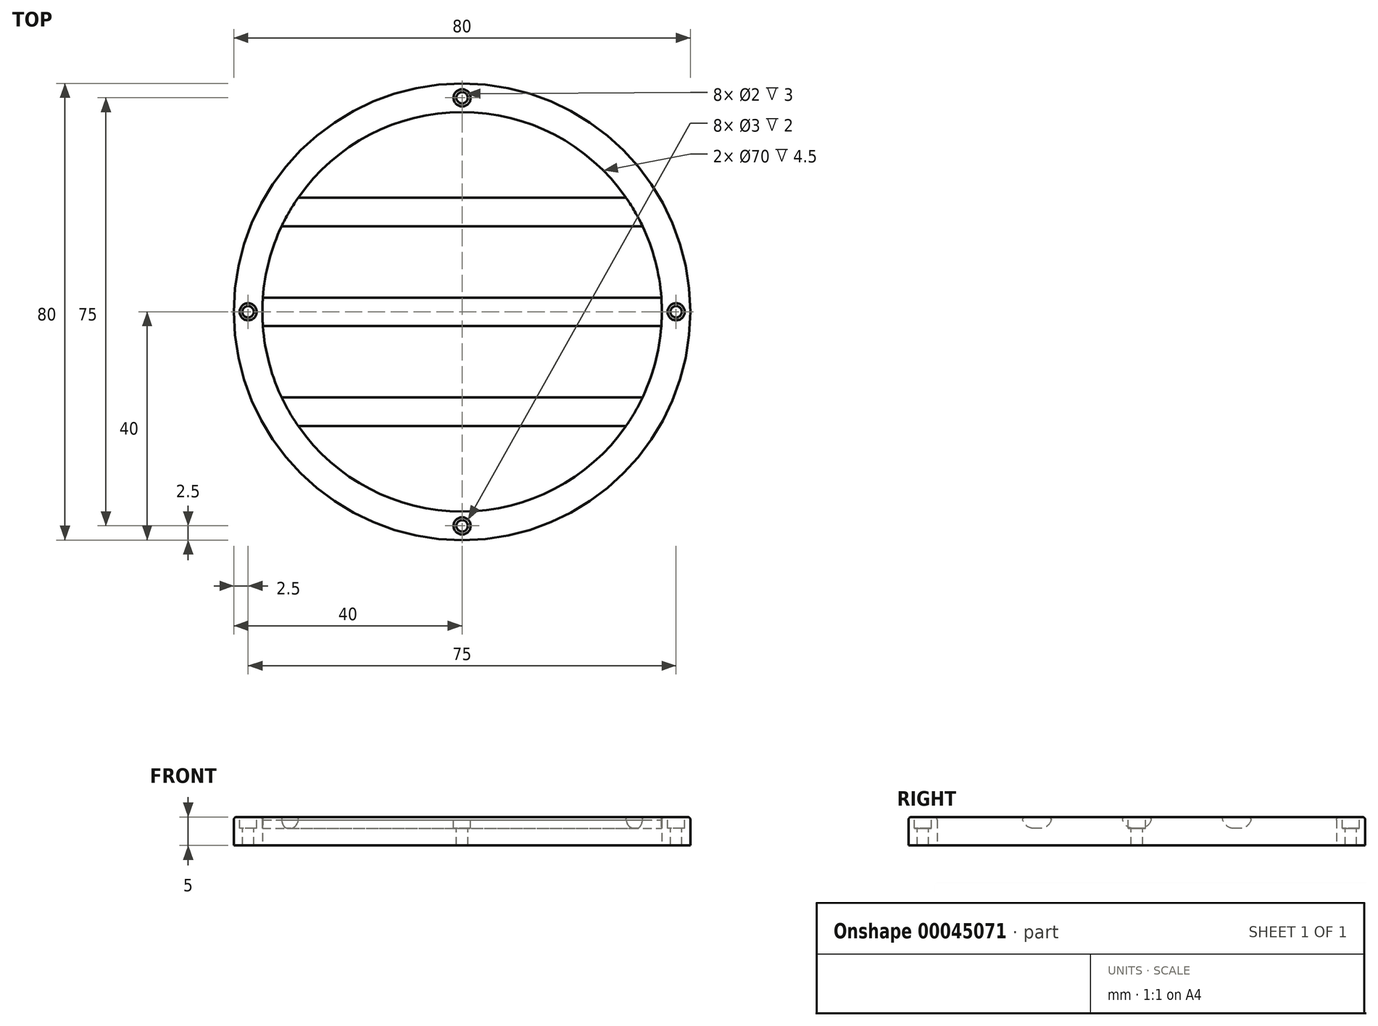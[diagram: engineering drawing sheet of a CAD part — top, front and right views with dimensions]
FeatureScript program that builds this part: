
annotation { "Feature Type Name" : "Feature", "Feature Type Description" : "" }
export const myFeature = defineFeature(function(context is Context, id is Id, definition is map)
    precondition{}
    {
        {
            var Q0;
            Q0=qCreatedBy(makeId("Top.planeOp"),FACE);
            var sketch = newSketch(context, id + "F0", { "sketchPlane" : qUnion([Q0])});
            skCircle(sketch, "E0", {"center": v(0, 0) * mm, "radius": 40 * mm});
            skCircle(sketch, "E1", {"center": v(0, 0) * mm, "radius": 35 * mm});
            skSolve(sketch);
        }
        {
            var Q0;
            Q0=makeQuery(id+"F0.imprint","IMPRINT",FACE,{"disambiguationData":[TD([[makeQuery(id+"F0.imprint","IMPRINT",EDGE,{"derivedFrom":sQuery(id+"F0.wireOp",EDGE,"E0")}),1.0]])]});
            extrude(context, id + "F1", {"entities" : qUnion([Q0]), "depth" : 5 * mm});
        }
        {
            var Q0;
            Q0=makeQuery(id+"F1.opExtrude","CAP_FACE",FACE,{"disambiguationData":[OSD([sQuery(id+"F0.wireOp",EDGE,"E0"),sQuery(id+"F0.wireOp",EDGE,"E1")])],"isStart":false});
            var sketch = newSketch(context, id + "F2", { "sketchPlane" : qUnion([Q0])});
            skLineSegment(sketch, "E2", {"start": v(-28.72, 20) * mm, "end": v(28.72, 20) * mm});
            skLineSegment(sketch, "E3", {"start": v(-31.62, 15) * mm, "end": v(31.62, 15) * mm});
            skLineSegment(sketch, "E4", {"start": v(-28.72, -20) * mm, "end": v(28.72, -20) * mm});
            skLineSegment(sketch, "E5", {"start": v(-31.62, -15) * mm, "end": v(31.62, -15) * mm});
            skLineSegment(sketch, "E6", {"start": v(-34.91, 2.5) * mm, "end": v(34.91, 2.5) * mm});
            skLineSegment(sketch, "E7", {"start": v(-34.91, -2.5) * mm, "end": v(34.91, -2.5) * mm});
            skSolve(sketch);
        }
        {
            var Q0;
            {var subQ2=sQuery(id+"F2.wireOp",EDGE,"E2");Q0=makeQuery(id+"F2.imprint","IMPRINT",FACE,{"disambiguationData":[TD([[makeQuery(id+"F2.imprint","IMPRINT",EDGE,{"derivedFrom":subQ2}),-1.0]])]});}
            var Q1;
            {var subQ2=sQuery(id+"F2.wireOp",EDGE,"E6");Q1=makeQuery(id+"F2.imprint","IMPRINT",FACE,{"disambiguationData":[TD([[makeQuery(id+"F2.imprint","IMPRINT",EDGE,{"derivedFrom":subQ2}),-1.0]])]});}
            var Q2;
            {var subQ2=sQuery(id+"F2.wireOp",EDGE,"E4");Q2=makeQuery(id+"F2.imprint","IMPRINT",FACE,{"disambiguationData":[TD([[makeQuery(id+"F2.imprint","IMPRINT",EDGE,{"derivedFrom":subQ2}),1.0]])]});}
            extrude(context, id + "F3", {"entities" : qUnion([Q0, Q1, Q2]), "oppositeDirection" : true, "depth" : 2 * mm});
        }
        {
            var Q0;
            Q0=makeQuery(id+"F1.opExtrude","CAP_FACE",FACE,{"disambiguationData":[OSD([sQuery(id+"F0.wireOp",EDGE,"E0"),sQuery(id+"F0.wireOp",EDGE,"E1")])],"isStart":false});
            var sketch = newSketch(context, id + "F4", { "sketchPlane" : qUnion([Q0])});
            skPoint(sketch, "E8", {"position": v(0, 37.5) * mm});
            skPoint(sketch, "E9", {"position": v(37.5, 0) * mm});
            skPoint(sketch, "E10", {"position": v(-37.5, 0) * mm});
            skPoint(sketch, "E11", {"position": v(0, -37.5) * mm});
            skSolve(sketch);
        }
        {
            var Q0;
            Q0=sQuery(id+"F4.wireOp",VERTEX,"E8");
            var Q1;
            Q1=sQuery(id+"F4.wireOp",VERTEX,"E9");
            var Q2;
            Q2=sQuery(id+"F4.wireOp",VERTEX,"E10");
            var Q3;
            Q3=sQuery(id+"F4.wireOp",VERTEX,"E11");
            var Q4;
            Q4=makeQuery(id+"F1.opExtrude","SWEPT_BODY",BODY,{"disambiguationData":[OSD([sQuery(id+"F0.wireOp",EDGE,"E0"),sQuery(id+"F0.wireOp",EDGE,"E1")])]});
            hole(context, id + "F5", {"style" : HoleStyle.C_BORE, "holeDiameter" : 2 * mm, "cBoreDiameter" : 3 * mm, "cBoreDepth" : 2 * mm, "endStyle" : HoleEndStyle.THROUGH, "locations" : qUnion([Q0, Q1, Q2, Q3]), "scope" : qUnion([Q4])});
        }
        {
            var Q0;
            Q0=makeQuery(id+"F1.opExtrude","CAP_EDGE",EDGE,{"disambiguationData":[OSD([sQuery(id+"F0.wireOp",EDGE,"E0")])],"isStart":false});
            var Q1;
            Q1=makeQuery(id+"F1.opExtrude","CAP_EDGE",EDGE,{"disambiguationData":[OSD([sQuery(id+"F0.wireOp",EDGE,"E1")])],"isStart":false});
            var Q2;
            Q2=makeQuery(id+"F5.hole-3.boolean.opBoolean","COPY",EDGE,{"derivedFrom":makeQuery(id+"F5.hole-3.opRevolve","SWEPT_EDGE",EDGE,{"disambiguationData":[OSD([sQuery(id+"F5.hole-3.sketch.wireOp",EDGE,"cbore_start_line_2"),sQuery(id+"F5.hole-3.sketch.wireOp",EDGE,"cbore_start_line_3")])]})});
            var Q3;
            Q3=makeQuery(id+"F3.opExtrude","CAP_EDGE",EDGE,{"disambiguationData":[OSD([sQuery(id+"F2.wireOp",EDGE,"E4")])],"isStart":true});
            var Q4;
            Q4=makeQuery(id+"F3.opExtrude","CAP_EDGE",EDGE,{"disambiguationData":[OSD([sQuery(id+"F2.wireOp",EDGE,"E5")])],"isStart":true});
            var Q5;
            Q5=makeQuery(id+"F3.opExtrude","CAP_EDGE",EDGE,{"disambiguationData":[OSD([sQuery(id+"F2.wireOp",EDGE,"E7")])],"isStart":true});
            var Q6;
            Q6=makeQuery(id+"F3.opExtrude","CAP_EDGE",EDGE,{"disambiguationData":[OSD([sQuery(id+"F2.wireOp",EDGE,"E6")])],"isStart":true});
            var Q7;
            Q7=makeQuery(id+"F3.opExtrude","CAP_EDGE",EDGE,{"disambiguationData":[OSD([sQuery(id+"F2.wireOp",EDGE,"E2")])],"isStart":true});
            var Q8;
            Q8=makeQuery(id+"F5.hole-2.boolean.opBoolean","COPY",EDGE,{"derivedFrom":makeQuery(id+"F5.hole-2.opRevolve","SWEPT_EDGE",EDGE,{"disambiguationData":[OSD([sQuery(id+"F5.hole-2.sketch.wireOp",EDGE,"cbore_start_line_2"),sQuery(id+"F5.hole-2.sketch.wireOp",EDGE,"cbore_start_line_3")])]})});
            var Q9;
            Q9=makeQuery(id+"F5.hole-1.boolean.opBoolean","COPY",EDGE,{"derivedFrom":makeQuery(id+"F5.hole-1.opRevolve","SWEPT_EDGE",EDGE,{"disambiguationData":[OSD([sQuery(id+"F5.hole-1.sketch.wireOp",EDGE,"cbore_start_line_2"),sQuery(id+"F5.hole-1.sketch.wireOp",EDGE,"cbore_start_line_3")])]})});
            var Q10;
            Q10=makeQuery(id+"F5.hole-0.boolean.opBoolean","COPY",EDGE,{"derivedFrom":makeQuery(id+"F5.hole-0.opRevolve","SWEPT_EDGE",EDGE,{"disambiguationData":[OSD([sQuery(id+"F5.hole-0.sketch.wireOp",EDGE,"cbore_start_line_2"),sQuery(id+"F5.hole-0.sketch.wireOp",EDGE,"cbore_start_line_3")])]})});
            fillet(context, id + "F6", {"entities" : qUnion([Q0, Q1, Q2, Q3, Q4, Q5, Q6, Q7, Q8, Q9, Q10]), "radius" : 0.5 * mm, "tangentPropagation" : true, "allowEdgeOverflow" : false});
        }
        {
            var Q0;
            Q0=makeQuery(id+"F3.opExtrude","CAP_EDGE",EDGE,{"disambiguationData":[OSD([sQuery(id+"F2.wireOp",EDGE,"E4")])],"isStart":false});
            var Q1;
            Q1=makeQuery(id+"F3.opExtrude","CAP_EDGE",EDGE,{"disambiguationData":[OSD([sQuery(id+"F2.wireOp",EDGE,"E5")])],"isStart":false});
            var Q2;
            Q2=makeQuery(id+"F3.opExtrude","CAP_EDGE",EDGE,{"disambiguationData":[OSD([sQuery(id+"F2.wireOp",EDGE,"E7")])],"isStart":false});
            var Q3;
            Q3=makeQuery(id+"F3.opExtrude","CAP_EDGE",EDGE,{"disambiguationData":[OSD([sQuery(id+"F2.wireOp",EDGE,"E6")])],"isStart":false});
            var Q4;
            Q4=makeQuery(id+"F3.opExtrude","CAP_EDGE",EDGE,{"disambiguationData":[OSD([sQuery(id+"F2.wireOp",EDGE,"E3")])],"isStart":false});
            var Q5;
            Q5=makeQuery(id+"F3.opExtrude","CAP_EDGE",EDGE,{"disambiguationData":[OSD([sQuery(id+"F2.wireOp",EDGE,"E2")])],"isStart":false});
            fillet(context, id + "F7", {"entities" : qUnion([Q0, Q1, Q2, Q3, Q4, Q5]), "radius" : 2 * mm, "tangentPropagation" : true, "allowEdgeOverflow" : false});
        }
    });
